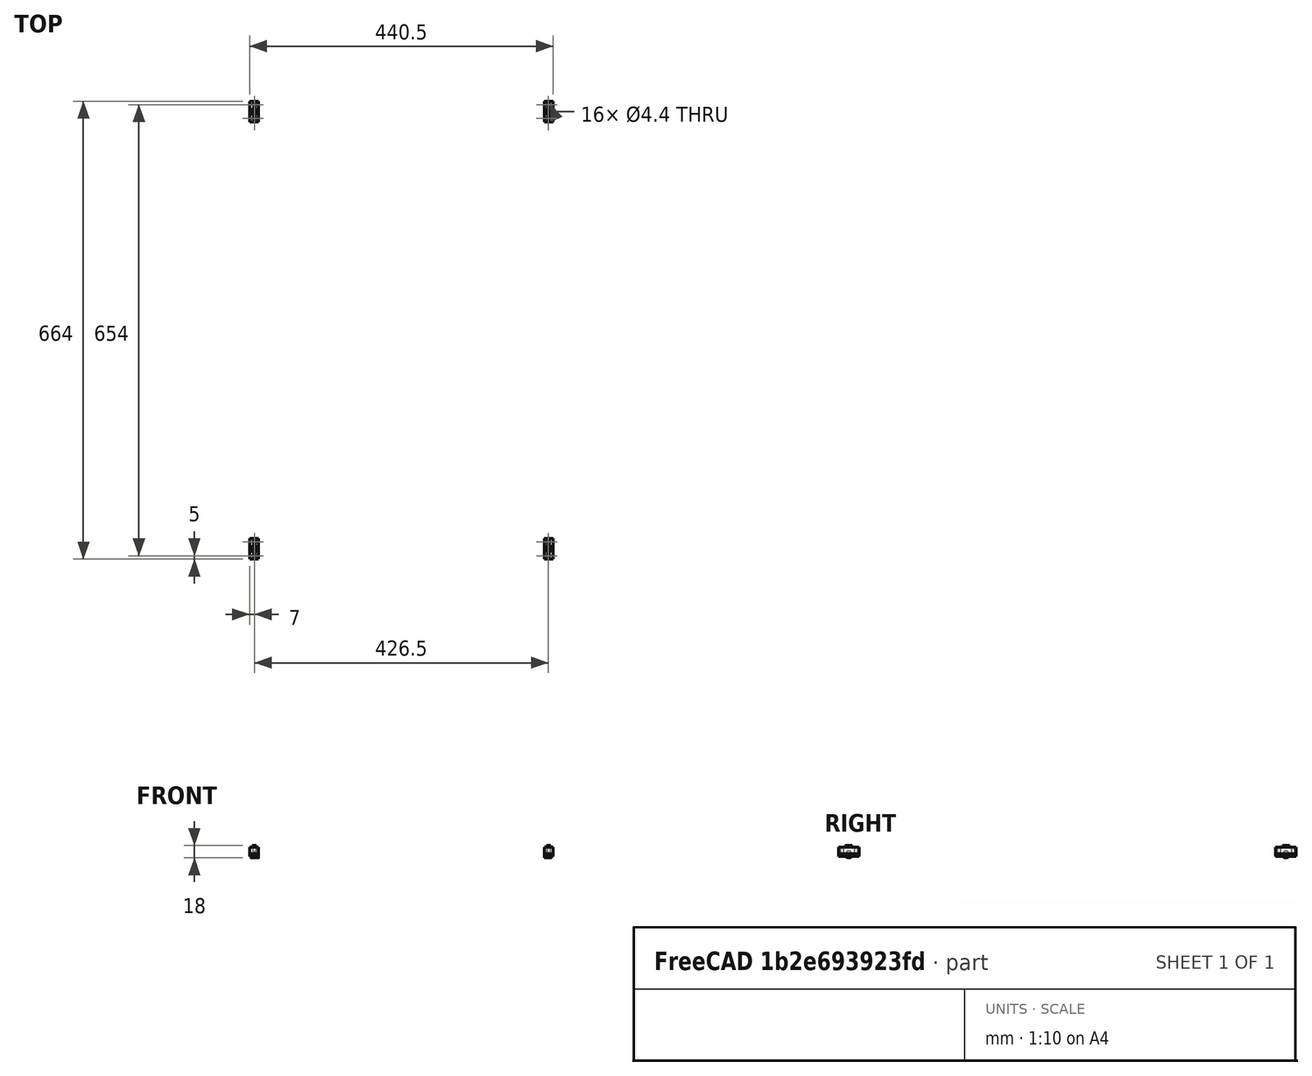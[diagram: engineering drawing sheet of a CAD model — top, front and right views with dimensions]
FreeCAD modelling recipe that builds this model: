
FCSTD DOCUMENT  (FreeCAD 0.18R16110 (Git))
Label: y-drive-mount
License: All rights reserved
LicenseURL: http://en.wikipedia.org/wiki/All_rights_reserved
objects: Part::Cut×9, Mesh::Feature×8, Part::Cylinder×7, Part::MultiFuse×5, Part::Box×3, Spreadsheet::Sheet×1
note: 24 computed .brp shape members not serialized (recipe doc carries the construction recipe); baked Part::Feature solids carry a one-line shape summary decoded from their .brp

FEATURE [Part::Cylinder] Cylinder073  label="Zylinder062"
  Angle = 360
  AttacherType = Attacher::AttachEngine3D
  Height = 20
  Placement = pos=(-10,9,5) rot=(1,0,0;1.5708rad)
  Radius = 2.2
FEATURE [Part::Cylinder] Cylinder077  label="Zylinder066"
  Angle = 360
  AttacherType = Attacher::AttachEngine3D
  Height = 25
  Placement = pos=(-10,12,5) rot=(1,0,0;1.5708rad)
  Radius = 2.2
FEATURE [Part::Box] Box054  label="Quader033"
  AttacherType = Attacher::AttachEngine3D
  Height = 13
  Length = 30
  Placement = pos=(-15,-3.7,-2) rot=(0,0,1;0rad)
  Width = 3.7
  expr: Placement.Base.y = -5 + 1.3
FEATURE [Part::Cylinder] Cylinder075  label="Zylinder064"
  Angle = 360
  AttacherType = Attacher::AttachEngine3D
  Height = 6
  Placement = pos=(0,0,5.8) rot=(0,0,1;0rad)
  Radius = 4
FEATURE [Part::Cylinder] Cylinder074  label="Zylinder063"
  Angle = 360
  AttacherType = Attacher::AttachEngine3D
  Height = 20
  Placement = pos=(10,9,5) rot=(1,0,0;1.5708rad)
  Radius = 2.2
FEATURE [Part::Cylinder] Cylinder071  label="Zylinder060"
  Angle = 180
  AttacherType = Attacher::AttachEngine3D
  Height = 11
  Placement = pos=(0,0,0) rot=(0,0,1;3.14159rad)
  Radius = 6
FEATURE [Part::MultiFuse] Fusion041
  Shapes = -> [Box054,Cylinder071]
FEATURE [Part::Cylinder] Cylinder072  label="Zylinder061"
  Angle = 360
  AttacherType = Attacher::AttachEngine3D
  Height = 6.5
  Placement = pos=(0,0,5.8) rot=(0,0,1;0rad)
  Radius = 4
FEATURE [Part::Cut] Cut081
  Base = -> Fusion041
  Tool = -> Cylinder072
FEATURE [Part::Cut] Cut082
  Base = -> Cut081
  Tool = -> Cylinder074
FEATURE [Part::Cut] Cut083  label="y-drive-mount-top001"
  Base = -> Cut082
  Placement = pos=(-32.75,18.85,53.2) rot=(0.57735,0.57735,0.57735;2.0944rad)
  Tool = -> Cylinder073
  expr: Placement.Base.z = Spreadsheet.E28 + Spreadsheet.E25 + Spreadsheet.F20 / 2 + Spreadsheet.tolerance * 4
  expr: Placement.Base.y = Spreadsheet.E27 + 15
  expr: Placement.Base.x = -(Spreadsheet.x_dlinear / 2 + Spreadsheet.y_df / 2 + Spreadsheet.K5 + Spreadsheet.K4) + 5
FEATURE [Part::Box] Box055  label="Quader034"
  AttacherType = Attacher::AttachEngine3D
  Height = 13
  Length = 30
  Placement = pos=(-15,0,-2) rot=(0,0,1;0rad)
  Width = 9.3
FEATURE [Part::Cut] Cut084
  Base = -> Box055
  Tool = -> Cylinder075
FEATURE [Part::Cylinder] Cylinder076  label="Zylinder065"
  Angle = 360
  AttacherType = Attacher::AttachEngine3D
  Height = 25
  Placement = pos=(10,12,5) rot=(1,0,0;1.5708rad)
  Radius = 2.2
FEATURE [Part::Cut] Cut085
  Base = -> Cut084
  Tool = -> Cylinder076
FEATURE [Part::Box] Box056  label="Quader035"
  AttacherType = Attacher::AttachEngine3D
  Height = 5.8
  Length = 10
  Placement = pos=(-5,8,2) rot=(0,0,1;0rad)
  Width = 4
  expr: Placement.Base.z = 2
FEATURE [Part::Cut] Cut089  label="y-drive-mount-top002"
  Base = -> Cut082
  Placement = pos=(-32.75,652.85,53.2) rot=(0.57735,0.57735,0.57735;2.0944rad)
  Tool = -> Cylinder073
  expr: Placement.Base.z = Spreadsheet.E28 + Spreadsheet.E25 + Spreadsheet.F20 / 2 + Spreadsheet.tolerance * 4
  expr: Placement.Base.y = Spreadsheet.E27 + Spreadsheet.y_fl - Spreadsheet.K4 + Spreadsheet.K5 * 2 - 2 - 20 - 15
  expr: Placement.Base.x = -(Spreadsheet.x_dlinear / 2 + Spreadsheet.y_df / 2 + Spreadsheet.K5 + Spreadsheet.K4) + 5
FEATURE [Part::Cut] Cut088  label="y-drive-mount-top003"
  Base = -> Cut082
  Placement = pos=(403.75,18.85,53.2) rot=(0.57735,-0.57735,-0.57735;2.0944rad)
  Tool = -> Cylinder073
  expr: Placement.Base.z = Spreadsheet.E28 + Spreadsheet.E25 + Spreadsheet.F20 / 2 + Spreadsheet.tolerance * 4
  expr: Placement.Base.y = Spreadsheet.E27 + 15
  expr: Placement.Base.x = -Spreadsheet.x_dlinear / 2 + Spreadsheet.y_sfa + Spreadsheet.x_df / 2 + Spreadsheet.K5 + 15
FEATURE [Part::Cut] Cut090  label="y-drive-mount-top004"
  Base = -> Cut082
  Placement = pos=(403.75,652.85,53.2) rot=(0.57735,-0.57735,-0.57735;2.0944rad)
  Tool = -> Cylinder073
  expr: Placement.Base.z = Spreadsheet.E28 + Spreadsheet.E25 + Spreadsheet.F20 / 2 + Spreadsheet.tolerance * 4
  expr: Placement.Base.y = Spreadsheet.E27 + Spreadsheet.y_fl - Spreadsheet.K4 + Spreadsheet.K5 * 2 - 2 - 20 - 15
  expr: Placement.Base.x = -Spreadsheet.x_dlinear / 2 + Spreadsheet.y_sfa + Spreadsheet.x_df / 2 + Spreadsheet.K5 + 15
FEATURE [Part::Cut] Cut086
  Base = -> Cut085
  Tool = -> Cylinder077
FEATURE [Part::MultiFuse] Fusion042  label="y-drive-mount001"
  Placement = pos=(-32.75,18.85,53.2) rot=(0.57735,0.57735,0.57735;2.0944rad)
  Shapes = -> [Cut086,Box056]
  expr: Placement.Base.y = Spreadsheet.E27 + 15
  expr: Placement.Base.x = -(Spreadsheet.x_dlinear / 2 + Spreadsheet.y_df / 2 + Spreadsheet.K5 + Spreadsheet.K4) + 5
  expr: Placement.Base.z = Spreadsheet.E28 + Spreadsheet.E25 + Spreadsheet.F20 / 2 + Spreadsheet.tolerance * 4
FEATURE [Part::MultiFuse] Fusion044  label="y-drive-mount002"
  Placement = pos=(403.75,18.85,53.2) rot=(0.57735,-0.57735,-0.57735;2.0944rad)
  Shapes = -> [Cut086,Box056]
  expr: Placement.Base.y = Spreadsheet.E27 + 15
  expr: Placement.Base.x = -Spreadsheet.x_dlinear / 2 + Spreadsheet.y_sfa + Spreadsheet.x_df / 2 + Spreadsheet.K5 + 15
  expr: Placement.Base.z = Spreadsheet.E28 + Spreadsheet.E25 + Spreadsheet.F20 / 2 + Spreadsheet.tolerance * 4
FEATURE [Part::MultiFuse] Fusion045  label="y-drive-mount003"
  Placement = pos=(-32.75,652.85,53.2) rot=(0.57735,0.57735,0.57735;2.0944rad)
  Shapes = -> [Cut086,Box056]
  expr: Placement.Base.y = Spreadsheet.E27 + Spreadsheet.y_fl - Spreadsheet.K4 + Spreadsheet.K5 * 2 - 2 - 20 - 15
  expr: Placement.Base.x = -(Spreadsheet.x_dlinear / 2 + Spreadsheet.y_df / 2 + Spreadsheet.K5 + Spreadsheet.K4) + 5
  expr: Placement.Base.z = Spreadsheet.E28 + Spreadsheet.E25 + Spreadsheet.F20 / 2 + Spreadsheet.tolerance * 4
FEATURE [Part::MultiFuse] Fusion046  label="y-drive-mount004"
  Placement = pos=(403.75,652.85,53.2) rot=(0.57735,-0.57735,-0.57735;2.0944rad)
  Shapes = -> [Cut086,Box056]
  expr: Placement.Base.y = Spreadsheet.E27 + Spreadsheet.y_fl - Spreadsheet.K4 + Spreadsheet.K5 * 2 - 2 - 20 - 15
  expr: Placement.Base.x = -Spreadsheet.x_dlinear / 2 + Spreadsheet.y_sfa + Spreadsheet.x_df / 2 + Spreadsheet.K5 + 15
  expr: Placement.Base.z = Spreadsheet.E28 + Spreadsheet.E25 + Spreadsheet.F20 / 2 + Spreadsheet.tolerance * 4
FEATURE [Spreadsheet::Sheet] Spreadsheet
  cells = A1=Toleranz; B1(tolerance)=0.2; D1=x_pos; E1=0; G1=y_pos; H1=0; A2=z_pos; B2=-10; E2=min 0 / max 297; G2=min y_pos; H2=94; I2=max 560; A3=Z-Support; D3=X-Support; G3=y-Support; J3=structure; A4=Führung d; B4(z_df)=8; D4=Führung d; E4(x_df)=10; G4=Führung d; H4(y_df)=10; J4=profil B; K4=20; A5=Führung l; B5(z_fl)==Spreadsheet.z_hub + Spreadsheet.z_hmount * 2 + Spreadsheet.z_hs - 5; D5=Führung l; E5(x_lf)=420; F5=400; G5=Führung l; H5(y_fl)=700; I5=500; J5=distanz Führung; K5=3; A6=Abstand Führung z_sfa; B6(z_sfa)==(z_dlinear + 2 * z_swand + 2 * z_sriemenspiel + z_lriemen) * 1 + (2 * x_hlinear + +z_swand - z_df + 4 * tolerance) * 0; D6=Abstand Führung x_sfa; E6(x_sfa)=65; G6=Abstand Fü y_sfa; H6(y_sfa)==x_lf - x_dlinear - 2 * y_swand; J6=höhe; K6=300; J7=add to Top; K7=18; A8=Schlittenwand swand; B8(z_swand)=5; D8=Schlitten swand; E8(x_swand)=4; G8=y_swand; H8(y_swand)=5; A9=Schlittenlänge z_ls; B9(z_ls)==z_sfa + z_dlinear; D9=Schlittenlänge; E9(x_ls)==z_lmount; A10=Schlittenbreite z_bs; B10(z_bs)==2 * z_swand + z_dlinear; D10=Schlitten breite; E10(x_bs)==Spreadsheet.x_swand * 2 + Spreadsheet.x_dlinear + Spreadsheet.x_sfa; G10=d Antrieb; H10=5; A11=Schlittenhöhe z_hs; B11(z_hs)==z_hlinear + 2 * z_swand; D11=schlittenhöhe x_hs; E11(x_hs)==x_dlinear + x_swand; A12=Hub; B12(z_hub)=100; A14=Linearlager; A15=durchmesser z_dlinear; B15(z_dlinear)=15.4; D15=durchmesser x_dlinear; E15(x_dlinear)=19.5; A16=höhe z_hlinear; B16(z_hlinear)=24.4; D16=höhe x_hlinear; E16(x_hlinear)=29.4; A18=Riemenscheibe bohrung; B18=5; A19=durchmesser z_driemen; B19(z_driemen)=16; D19=dopper pulley; E19=27.5; F19=15.8; A20=länge z_lriemen; B20(z_lriemen)=28; D20=pulley; E20=15.25; F20=15.8; G20=20 Zähne: 2* 180 °; H20=2mm*20 Zähne; I20==40mm; A21=spiel riemenscheibe z_sriemenspiel; B21(z_sriemenspiel)=2; A22=Bohreung z_dbohrung; B22(z_dbohrung)=8; C22=durchmesser Laufbuchse; D22=x_mount; A23=Bohrunlänge z_lbohrung; B23(z_lbohrung)=5; D23=Breite x_mount; E23==y_swand + x_dlinear; A24=riemenbreite z_briemen; B24(z_briemen)=6; D24=Länge x_mount; E24==x_sfa + x_df + y_swand * 2; A25=pitch z_rriemenpitch; B25(z_rriemepitch)=7; D25=Höhe x_mount; E25==y_swand * 2 + x_df + +y_swand + x_dlinear + y_swand; A26=achsen pos y; B26==-Spreadsheet.z_driemen / 2 - Spreadsheet.tolerance * 2; D26= xpos; E26==-Spreadsheet.E23; A27=achsen pos z; B27==(Spreadsheet.z_hub + Spreadsheet.z_hs + Spreadsheet.x_hs) / 2 + z_hmount - z_dbohrung / 2 - Spreadsheet.z_dbohrung / 2; D27=ypos; E27==Spreadsheet.x_swand + Spreadsheet.x_dlinear / 2 + Spreadsheet.tolerance / 2 - Spreadsheet.x_df / 2 - Spreadsheet.y_swand; D28= zpos; E28==-y_swand; A29=Mount; A30=Höhe mount; B30(z_hmount)=20; A31=Länge mount; B31(z_lmount)==z_swand * 2 + z_df + z_sfa; A32=Breite mount; B32(z_bmount)==(Spreadsheet.z_swand + Spreadsheet.z_driemen + Spreadsheet.tolerance * 2) * 0 + 26; A34=Nema; D34=Nema x; A35=Länge; B35(lnema)=42; D35(nema_x_b)=42; A36=Breite; B36(bnema)=42; D36=42; A37=Höhe; B37(hnema)=34; D37(nema_x_h)=48; A38=Achslänge; B38(lanema)=20; D38(nema_x_al)=22; A39=achsen pos y; B39(nema_achse_y)==sqrt(B43 ^ 2 - (B27 - B40) ^ 2) + B26; E39(nemax_achsey)==Spreadsheet.x_swand + Spreadsheet.x_df / 2 + Spreadsheet.x_dlinear / 2 + Spreadsheet.nema_x_h + 2; A40=achsen pos z; B40(nema_achse_z)==x_hs + lnema / 2 + 4; E40(nema_x_achsez)==-Spreadsheet.x_hs / 2; A41=achsen pos x; B41(nema_achse_x)==(z_lmount - z_lriemen) / 2 - z_sriemenspiel; E41(nema_x_achsex)==Spreadsheet.x_lf - Spreadsheet.nema_x_b / 2 - Spreadsheet.y_df; A42=länge zahnriemen; B42=200; C42=gerechnet; A43=abstand achsen; B43==(B42 - 40) / 2; C43==sqrt((Spreadsheet.B27 - Spreadsheet.nema_achse_z) ^ 2 + (-Spreadsheet.B26 + Spreadsheet.nema_achse_y) ^ 2) * 2 + 2 * pi * 7; D43=Zahnriemen x; D44=Breite; E44=6; A45=doppel pulley; D45=Höhe; E45==(Spreadsheet.F20 + Spreadsheet.tolerance * 2) * 0 + 15; A46= achse1  x pos; B46==z_lmount / 2 - (6.5 + 8.9) / 2; D46=Länge; E46==y_sfa + x_dlinear + y_swand * 2 + 2 + nema_x_b / 2; A47= achse2 xpos; B47==z_lmount / 2 + (6.5 + 8.9) / 2; B48==-atan((Spreadsheet.B27 - Spreadsheet.nema_achse_z) / (-Spreadsheet.B26 + Spreadsheet.nema_achse_y))
FEATURE [Mesh::Feature] Mesh  label="y-drive-mount001 (Meshed)"
FEATURE [Mesh::Feature] Mesh001  label="y-drive-mount002 (Meshed)"
FEATURE [Mesh::Feature] Mesh002  label="y-drive-mount003 (Meshed)"
FEATURE [Mesh::Feature] Mesh003  label="y-drive-mount004 (Meshed)"
FEATURE [Mesh::Feature] Mesh004  label="y-drive-mount-top001 (Meshed)"
FEATURE [Mesh::Feature] Mesh005  label="y-drive-mount-top002 (Meshed)"
FEATURE [Mesh::Feature] Mesh006  label="y-drive-mount-top003 (Meshed)"
FEATURE [Mesh::Feature] Mesh007  label="y-drive-mount-top004 (Meshed)"
